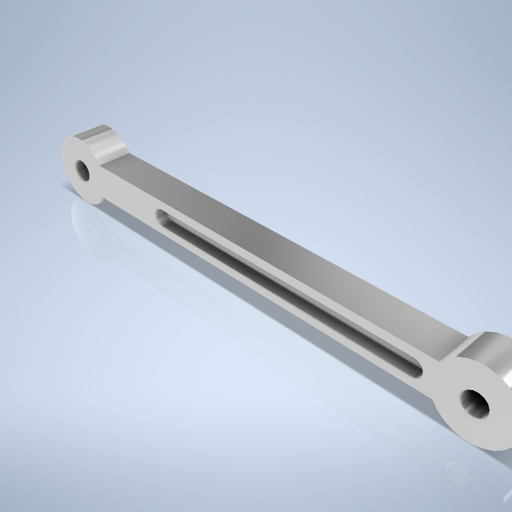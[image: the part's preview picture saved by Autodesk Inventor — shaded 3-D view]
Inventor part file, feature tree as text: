
AUTODESK INVENTOR PART (.ipt)
format: ipt  version: 2024.2 (Build 282272000, 272)  size: 305,664 bytes
history: native  units: mm
features: sketch x6, extrude x3, plane x3, hole x3, mirror x1
ambient origin geometry x8: Origin, YZ Plane, XZ Plane, XY Plane, X Axis, Y Axis, Z Axis, Center Point
bodies: Volumenkörper1 (feature_tree)
feature tree (16):
  extrude  "Extrusion1"  Depth=12.0mm
  plane  "Arbeitsebene1"
  extrude  "Extrusion2"  Depth=150.0mm
  hole  "Bohrung1"  [1 undecoded]
  extrude  "Extrusion3"  Depth=12.0mm TaperAngle=0.0deg
  mirror  "Spiegeln1"
  plane  "Arbeitsebene2"
  hole  "Bohrung2"  [1 undecoded]
  plane  "Arbeitsebene3"
  hole  "Bohrung3"  [1 undecoded]
  sketch  "Skizze1"  dims[d0=24.0mm d1=12.0mm]
  sketch  "Skizze2"  dims[d2=7.5mm d3=150.0mm]
  sketch  "Skizze3"  dims[d4=12.0mm d5=0.0mm d6=0.0mm]
  sketch  "Skizze4"  dims[d7=24.0mm d9=12.0mm d10=0.0mm]
  sketch  "Skizze5"  dims[d11=7.5mm d12=6.0mm d13=4.0mm d14=2.0mm d15=90.0deg d16=8.0mm d17=20.594885mm d18=6.0mm]
  sketch  "Skizze6"  dims[d20=98.0mm d21=150.0mm d22=14.0mm d23=4.0mm d24=0.0mm d25=12.0mm d26=4.5mm d27=6.0mm d28=4.0mm d29=2.0mm d30=90.0deg d31=5.5mm d32=20.594885mm d33=-142.5mm d34=4.5mm d35=6.0mm d36=4.0mm d37=2.0mm d38=90.0deg d39=5.5mm d40=20.594885mm]
note: 3 required parameter values undecoded (feature->parameter linkage not recoverable at this tier; creation-order binding heuristic only, values carry confidence <= 0.55)
